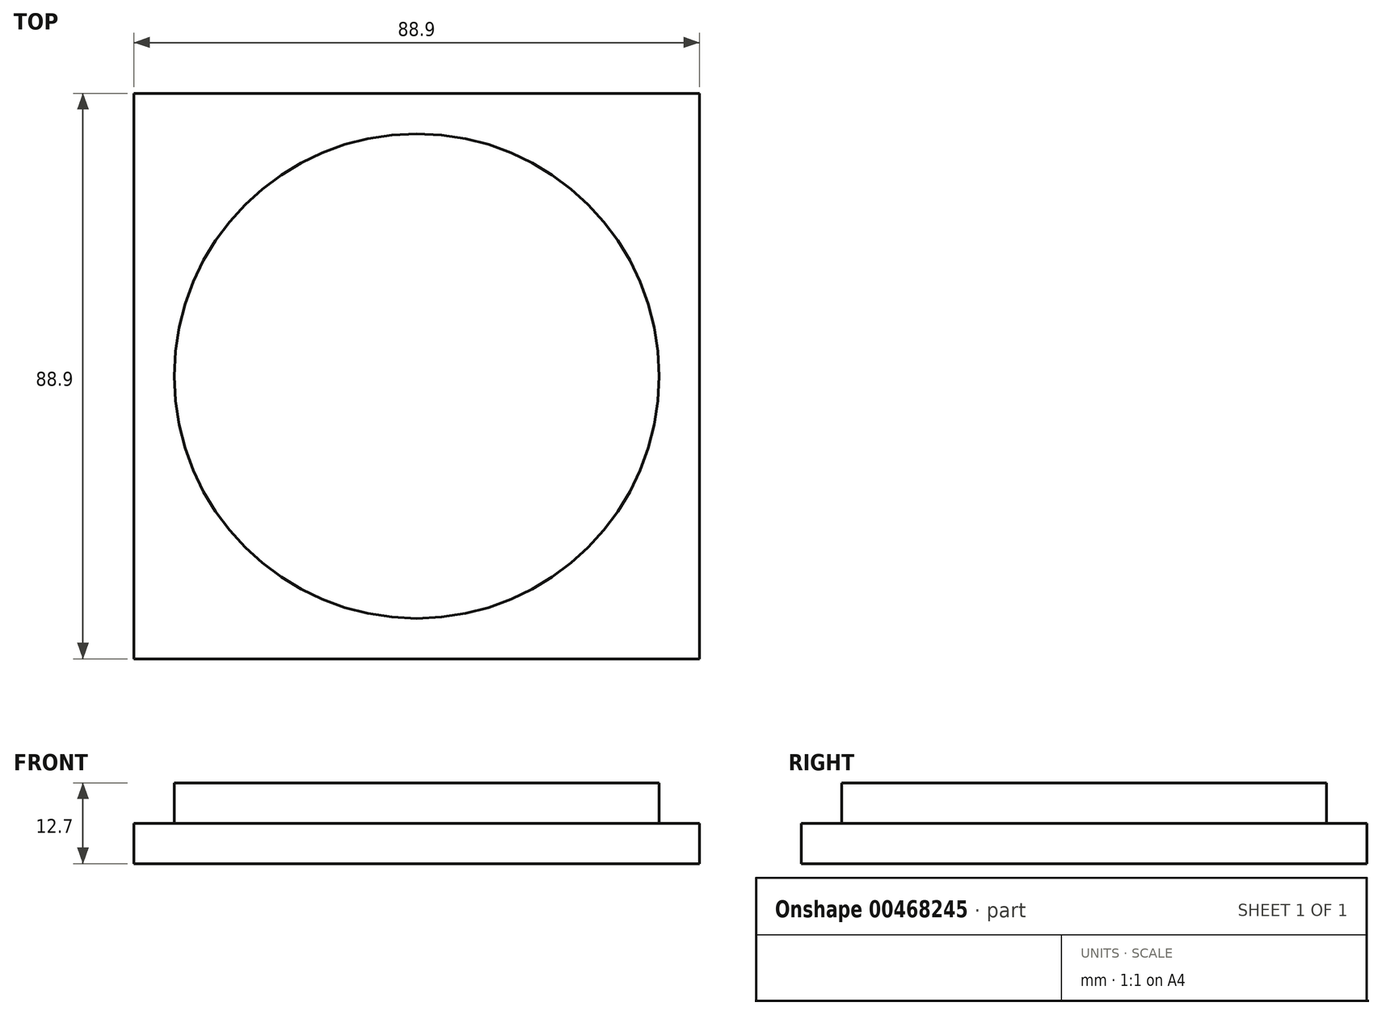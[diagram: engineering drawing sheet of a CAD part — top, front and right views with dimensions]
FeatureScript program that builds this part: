
annotation { "Feature Type Name" : "Feature", "Feature Type Description" : "" }
export const myFeature = defineFeature(function(context is Context, id is Id, definition is map)
    precondition{}
    {
        {
            var Q0;
            Q0=qCreatedBy(makeId("Top.planeOp"),FACE);
            var sketch = newSketch(context, id + "F0", { "sketchPlane" : qUnion([Q0])});
            skCircle(sketch, "E0", {"center": v(0, 0) * mm, "radius": 38.1 * mm});
            skSolve(sketch);
        }
        {
            var Q0;
            Q0=qSketchRegion(id+"F0",true);
            extrude(context, id + "F1", {"entities" : qUnion([Q0]), "depth" : 6.35 * mm});
        }
        {
            var Q0;
            Q0=qCreatedBy(makeId("Top.planeOp"),FACE);
            var sketch = newSketch(context, id + "F2", { "sketchPlane" : qUnion([Q0])});
            skLineSegment(sketch, "E1.bottom", {"start": v(-44.45, 44.45) * mm, "end": v(44.45, 44.45) * mm});
            skLineSegment(sketch, "E1.top", {"start": v(-44.45, -44.45) * mm, "end": v(44.45, -44.45) * mm});
            skLineSegment(sketch, "E1.left", {"start": v(-44.45, 44.45) * mm, "end": v(-44.45, -44.45) * mm});
            skLineSegment(sketch, "E1.right", {"start": v(44.45, 44.45) * mm, "end": v(44.45, -44.45) * mm});
            skPoint(sketch, "E2", {"position": v(0, 44.45) * mm});
            skPoint(sketch, "E3", {"position": v(-44.45, 0) * mm});
            skSolve(sketch);
        }
        {
            var Q0;
            Q0=qSketchRegion(id+"F2",true);
            extrude(context, id + "F3", {"entities" : qUnion([Q0]), "operationType" : NewBodyOperationType.ADD, "oppositeDirection" : true, "depth" : 6.35 * mm});
        }
    });
